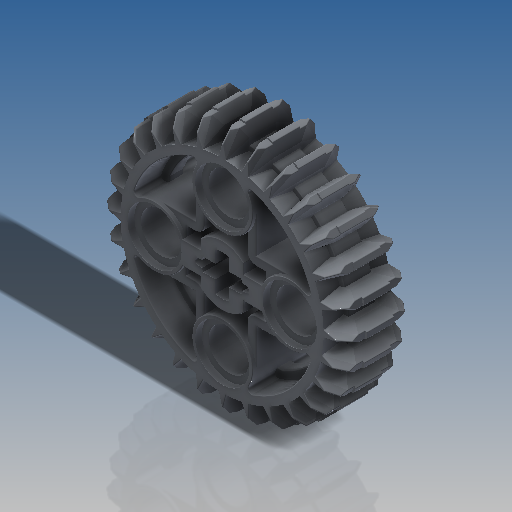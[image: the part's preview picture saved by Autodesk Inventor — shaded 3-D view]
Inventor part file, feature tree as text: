
AUTODESK INVENTOR PART (.ipt)
format: ipt  version: 2019 (Build 230136000, 136)  size: 5,972,480 bytes
history: native  units: in
note: dims shown in document units (in); Inventor stores cm internally (conversion verified against a paired STEP export)
features: extrude x8, sketch x7, fillet x3, loft x2, plane x1, mirror x1, pattern_circular x1, other x1
ambient origin geometry x8: Origin, YZ Plane, XZ Plane, XY Plane, X Axis, Y Axis, Z Axis, Center Point
bodies: Solid1 (feature_tree)
feature tree (24):
  sketch  "Sketch2"  dims[d0=0.6299in d1=0.189in]
  extrude  "Extrusion1"  Depth=0.189in
  extrude  "Extrusion2"  Depth=0.2835in
  extrude  "Extrusion3"  Depth=0.189in
  extrude  "Extrusion4"  Depth=0.0039in
  extrude  "Extrusion5"  Depth=0.0039in
  extrude  "Extrusion6"  Depth=0.0039in
  fillet  "Fillet1"  Radius=0.252in
  fillet  "Fillet2"  Radius=0.8661in
  sketch  "Sketch4"  dims[d2=0.252in d3=0.2835in]
  plane  "Work Plane1"
  sketch  "Sketch5"  dims[d4=0.2835in d5=0.189in]
  loft  "Loft1"
  extrude  "Extrusion8"  Depth=0.0039in
  loft  "Loft4"
  mirror  "Mirror2"
  extrude  "Extrusion9"  Depth=0.0039in
  fillet  "Fillet3"  Radius=0.7387in
  pattern_circular  "Circular Pattern1"  [2 undecoded]
  sketch  "Sketch8"  dims[d6=0.2004in d8=0.1417in d9=0.063in d10=0.0315in d11=0.252in d12=0.8661in d13=0.2004in d14=0.368in d15=0.7992in d16=0.9449in d17=0.9896in d18=0.7387in d19=0.7992in d20=0.8661in d21=0.0269in d22=0.0648in d23=0.5796in d24=0.5229in d25=0.315in d26=0.0in d27=0.315in d28=0.0in d29=0.252in d30=0.0in d31=0.2835in d32=0.0in d33=0.126in d34=0.0in d35=0.063in d36=0.0in d37=0.0157in d38=0.0039in d39=0.0039in d42=0.5391in d43=0.0324in d44=0.0081in d45=0.0in d46=0.126in d47=0.0945in d48=0.0in d49=90.0deg d50=0.0in d51=90.0deg d58=0.063in d59=0.0in d72=0.0in d73=90.0deg d74=0.0in d75=90.0deg d76=0.0in d77=90.0deg d78=0.0in d79=90.0deg d80=0.0in d81=90.0deg d82=0.0in d83=90.0deg d84=0.0in d85=90.0deg d86=0.0in d87=90.0deg d88=0.0in d89=90.0deg d90=0.0in d91=90.0deg d92=0.063in d93=0.0in d94=0.0039in d95=11.0236in d96=360.0deg d98=0.0in d99=0.0in d100=0.0in]
  sketch  "3D Sketch4"
  sketch  "3D Sketch5"
  sketch  "3D Sketch6"
  other  "Edges4"
note: 2 required parameter values undecoded (feature->parameter linkage not recoverable at this tier; creation-order binding heuristic only, values carry confidence <= 0.55)
